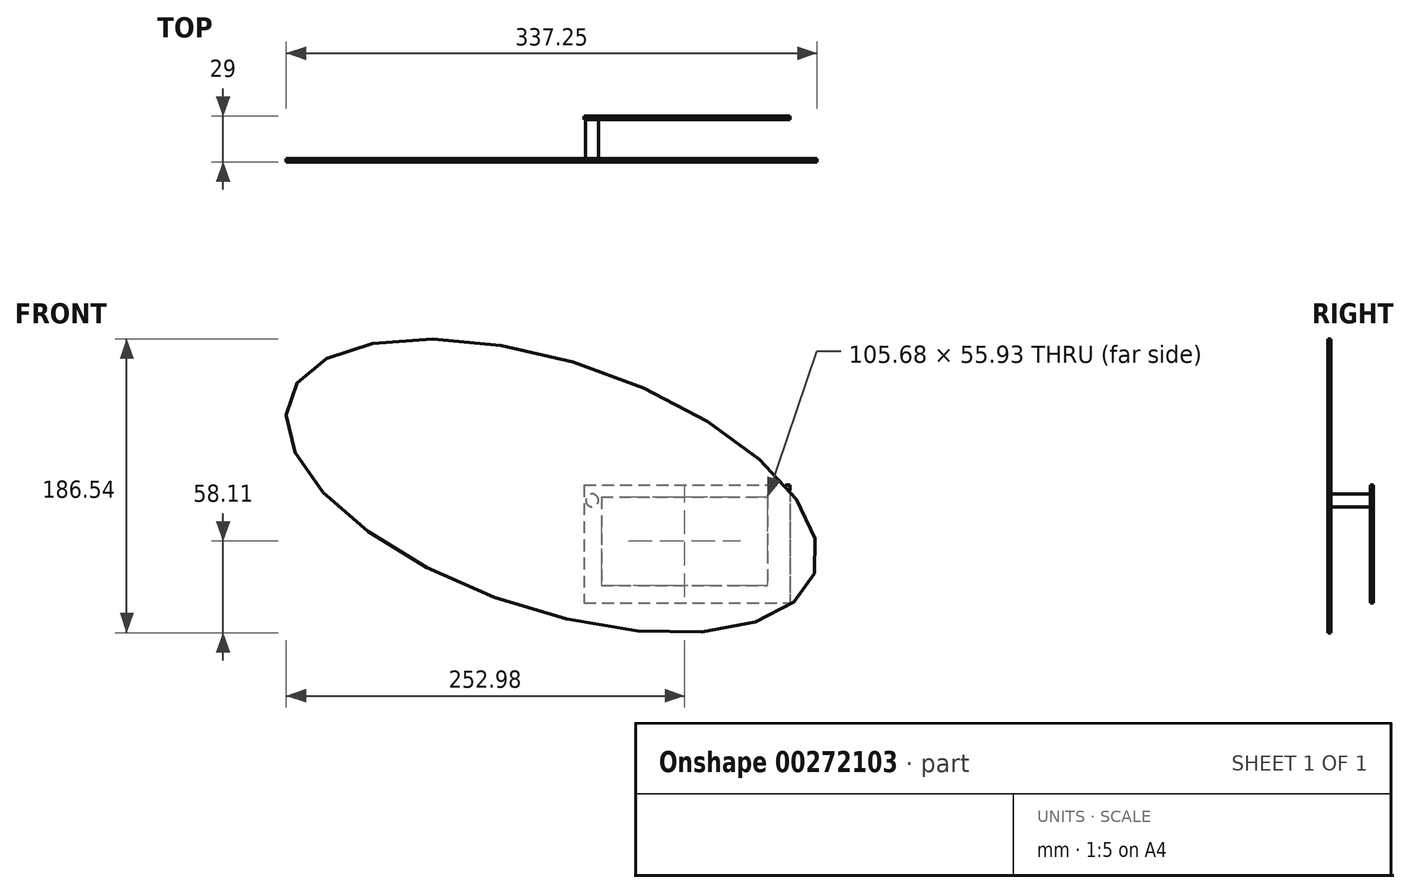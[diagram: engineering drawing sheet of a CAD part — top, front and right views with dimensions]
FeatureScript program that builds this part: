
annotation { "Feature Type Name" : "Feature", "Feature Type Description" : "" }
export const myFeature = defineFeature(function(context is Context, id is Id, definition is map)
    precondition{}
    {
        {
            var Q0;
            Q0=qCreatedBy(makeId("Front.planeOp"),FACE);
            var sketch = newSketch(context, id + "F0", { "sketchPlane" : qUnion([Q0])});
            skLineSegment(sketch, "E0.bottom", {"start": v(-63.8, 40.93) * mm, "end": v(66.83, 40.93) * mm});
            skLineSegment(sketch, "E0.top", {"start": v(-63.8, -34.01) * mm, "end": v(66.83, -34.01) * mm});
            skLineSegment(sketch, "E0.left", {"start": v(-63.8, 40.93) * mm, "end": v(-63.8, -34.01) * mm});
            skLineSegment(sketch, "E0.right", {"start": v(66.83, 40.93) * mm, "end": v(66.83, -34.01) * mm});
            skLineSegment(sketch, "E1.bottom", {"start": v(-52.84, 33.3) * mm, "end": v(52.84, 33.3) * mm});
            skLineSegment(sketch, "E1.top", {"start": v(-52.84, -22.63) * mm, "end": v(52.84, -22.63) * mm});
            skLineSegment(sketch, "E1.left", {"start": v(-52.84, 33.3) * mm, "end": v(-52.84, -22.63) * mm});
            skLineSegment(sketch, "E1.right", {"start": v(52.84, 33.3) * mm, "end": v(52.84, -22.63) * mm});
            skSolve(sketch);
        }
        {
            var Q0;
            Q0 = qSketchRegion(id + "F0", true);
            extrude(context, id + "F1", {"entities" : qUnion([Q0]), "depth" : 2 * mm});
        }
        {
            var Q0;
            Q0=makeQuery(id+"F1.opExtrude","CAP_FACE",FACE,{"disambiguationData":[OSD([sQuery(id+"F0.wireOp",EDGE,"E0.bottom"),sQuery(id+"F0.wireOp",EDGE,"E0.top"),sQuery(id+"F0.wireOp",EDGE,"E0.left"),sQuery(id+"F0.wireOp",EDGE,"E0.right"),sQuery(id+"F0.wireOp",EDGE,"E1.bottom"),sQuery(id+"F0.wireOp",EDGE,"E1.top"),sQuery(id+"F0.wireOp",EDGE,"E1.left"),sQuery(id+"F0.wireOp",EDGE,"E1.right")])],"isStart":false});
            var sketch = newSketch(context, id + "F2", { "sketchPlane" : qUnion([Q0])});
            skCircle(sketch, "E2", {"center": v(-58.67, 31.24) * mm, "radius": 4.04 * mm});
            skSolve(sketch);
        }
        {
            var Q0;
            Q0 = qSketchRegion(id + "F2", true);
            extrude(context, id + "F3", {"entities" : qUnion([Q0]), "operationType" : NewBodyOperationType.ADD, "depth" : 25 * mm});
        }
        {
            var Q0;
            Q0=makeQuery(id+"F3.opExtrude","CAP_FACE",FACE,{"disambiguationData":[OSD([sQuery(id+"F2.wireOp",EDGE,"E2")])],"isStart":false});
            var sketch = newSketch(context, id + "F4", { "sketchPlane" : qUnion([Q0])});
            skEllipse(sketch, "E3", {"center": v(-84.36, 40.5) * mm, "majorRadius": 175.8 * mm, "minorRadius": 78.94 * mm, "majorAxis": v(0.95, -0.32)});
            skSolve(sketch);
        }
        {
            var Q0;
            Q0 = qSketchRegion(id + "F4", true);
            extrude(context, id + "F5", {"entities" : qUnion([Q0]), "depth" : 2 * mm});
        }
    });
